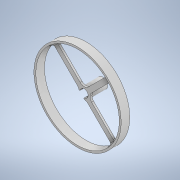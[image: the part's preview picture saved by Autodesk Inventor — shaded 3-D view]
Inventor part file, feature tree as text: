
AUTODESK INVENTOR PART (.ipt)
format: ipt  version: 2020 (Build 240168000, 168)  size: 424,448 bytes
history: native  units: in
note: dims shown in document units (in); Inventor stores cm internally (conversion verified against a paired STEP export)
features: fillet x4, extrude x3, sketch x3
ambient origin geometry x8: Origin, YZ Plane, XZ Plane, XY Plane, X Axis, Y Axis, Z Axis, Center Point
bodies: Solid1 (feature_tree)
feature tree (10):
  extrude  "Extrusion1"  Depth=0.4224in
  extrude  "Extrusion2"  Depth=0.748in TaperAngle=0.0deg
  extrude  "Extrusion3"  Depth=0.1181in
  fillet  "Fillet1"  Radius=0.0787in
  fillet  "Fillet2"  Radius=1.5748in
  fillet  "Fillet3"  Radius=3.4252in
  fillet  "Fillet4"  Radius=3.5827in
  sketch  "Sketch1"  dims[d0=0.3248in d1=0.4224in]
  sketch  "Sketch2"  dims[d2=0.7696in d3=0.748in d4=0.0in]
  sketch  "Sketch3"  dims[d5=1.063in d6=1.063in d7=0.0787in d8=0.0in d9=1.5748in d11=360.0deg d13=3.4252in d14=3.5827in d15=0.2756in d16=0.0in d17=0.0787in d18=0.0in d19=0.2362in d20=0.2362in d21=0.0787in d22=0.1181in]
